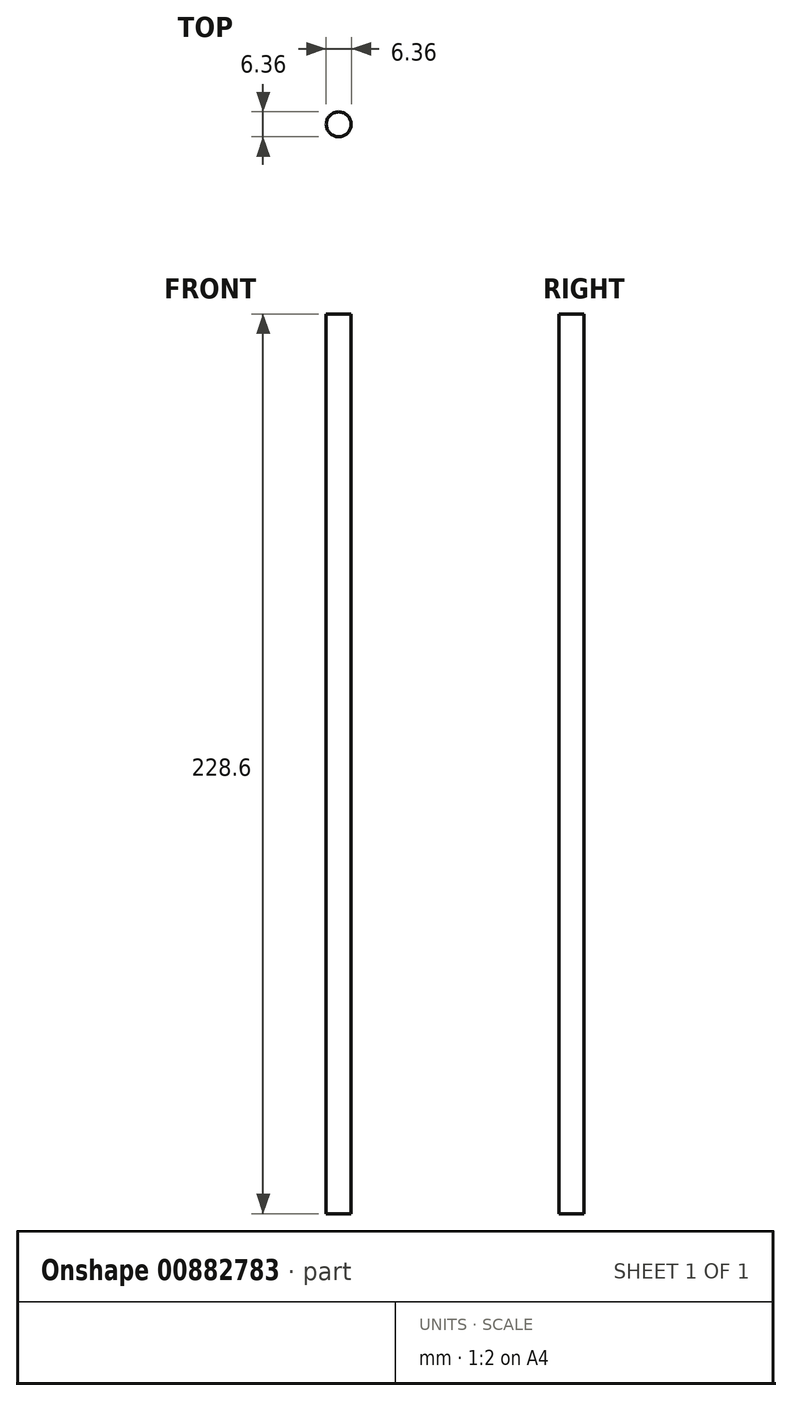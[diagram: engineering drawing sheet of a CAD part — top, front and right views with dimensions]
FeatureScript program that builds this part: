
annotation { "Feature Type Name" : "Feature", "Feature Type Description" : "" }
export const myFeature = defineFeature(function(context is Context, id is Id, definition is map)
    precondition{}
    {
        {
            var Q0;
            Q0=qCreatedBy(makeId("Top.planeOp"),FACE);
            var sketch = newSketch(context, id + "F0", { "sketchPlane" : qUnion([Q0])});
            skCircle(sketch, "E0", {"center": v(0, 0) * mm, "radius": 3.18 * mm});
            skSolve(sketch);
        }
        {
            var Q0;
            Q0 = qSketchRegion(id + "F0", true);
            extrude(context, id + "F1", {"entities" : qUnion([Q0]), "depth" : 228.6 * mm, "offsetDistance" : 25.4 * mm});
        }
    });
